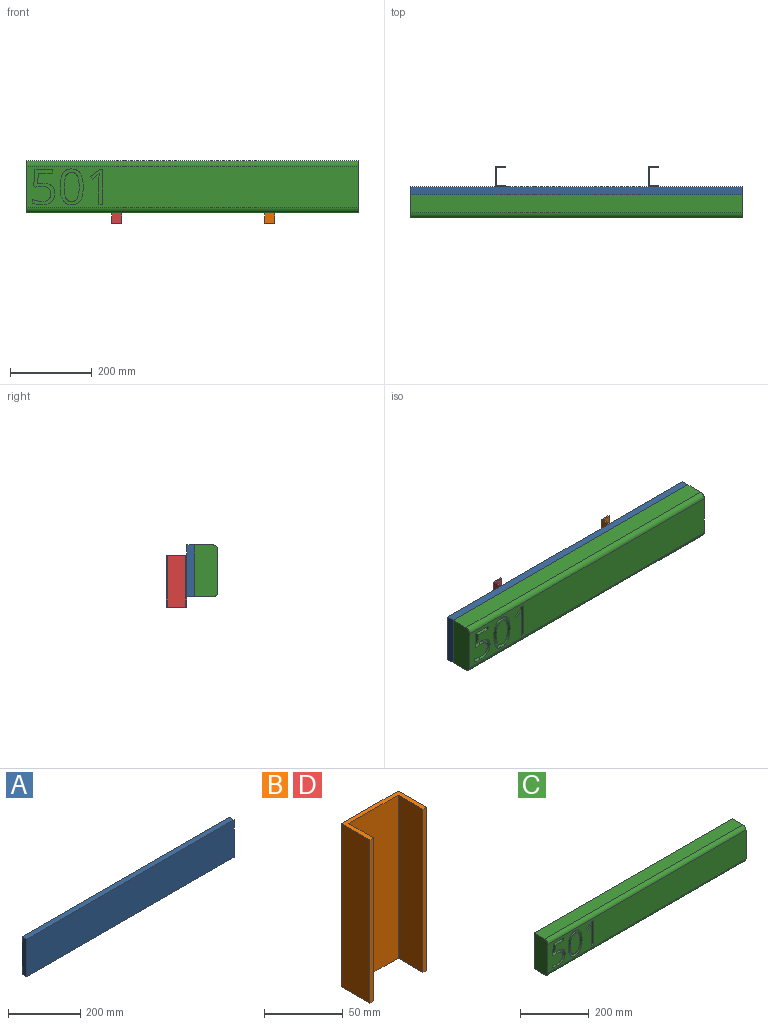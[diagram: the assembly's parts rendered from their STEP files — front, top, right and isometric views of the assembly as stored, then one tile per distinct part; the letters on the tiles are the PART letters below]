
ASSEMBLY  parts=4 mates=3
PART A: 6 faces, bbox 812.8x19.1x127 mm
  f0: plane 127x19.05mm, normal (1,0,0), area 2419.3mm2, adj f1,f3,f4,f5
  f1: plane 812.8x19.05mm, normal (0,0,1), area 15483.8mm2, adj f0,f2,f4,f5
  f2: plane 127x19.05mm, normal (-1,0,0), area 2419.3mm2, adj f1,f3,f4,f5
  f3: plane 812.8x19.05mm, normal (0,0,-1), area 15483.8mm2, adj f0,f2,f4,f5
  f4: plane 812.8x127mm, normal (0,-1,0), area 103225.6mm2, adj f0,f1,f2,f3
  f5: plane 812.8x127mm, normal (0,1,0), area 103225.6mm2, adj f0,f1,f2,f3
PART B: 10 faces, bbox 50.8x25.4x127 mm
  f0: plane 127x3.18mm, normal (0,-1,0), area 403.2mm2, adj f1,f6,f8,f9
  f1: plane 127x22.23mm, normal (1,0,0), area 2822.6mm2, adj f0,f2,f8,f9
  f2: plane 127x44.45mm, normal (0,-1,0), area 5645.2mm2, adj f1,f3,f8,f9
  f3: plane 127x22.23mm, normal (-1,0,0), area 2822.6mm2, adj f2,f7,f8,f9
  f4: plane 127x25.4mm, normal (1,0,0), area 3225.8mm2, adj f5,f7,f8,f9
  f5: plane 127x50.8mm, normal (0,1,0), area 6451.6mm2, adj f4,f6,f8,f9
  f6: plane 127x25.4mm, normal (-1,0,0), area 3225.8mm2, adj f0,f5,f8,f9
  f7: plane 127x3.18mm, normal (0,-1,0), area 403.2mm2, adj f3,f4,f8,f9
  f8: plane 50.8x25.4mm, normal (0,0,1), area 302.4mm2, adj f0,f1,f2,f3,f4,f5,f6,f7
  f9: plane 50.8x25.4mm, normal (0,0,-1), area 302.4mm2, adj f0,f1,f2,f3,f4,f5,f6,f7
PART C: 56 faces, bbox 812.8x57.2x127 mm
  f0: plane 812.8x101.6mm, normal (0,-1,0), area 75725.7mm2, adj f1,f3,f6,f7,f15,f16,f17,f18
  f1: plane 127x57.15mm, normal (1,0,0), area 7188.8mm2, adj f0,f2,f4,f5,f6,f7
  f2: plane 812.8x44.45mm, normal (0,0,1), area 36129mm2, adj f1,f3,f5,f6
  f3: plane 127x57.15mm, normal (-1,0,0), area 7188.8mm2, adj f0,f2,f4,f5,f6,f7
  f4: plane 812.8x44.45mm, normal (0,0,-1), area 36129mm2, adj f1,f3,f5,f7
  f5: plane 812.8x127mm, normal (0,1,0), area 103225.6mm2, adj f1,f2,f3,f4
  f6: cylinder r=12.7mm len=812.8mm, axis (1,0,0), area 16214.6mm2, adj f0,f1,f2,f3
  f7: cylinder r=12.7mm len=812.8mm, axis (-1,0,0), area 16214.6mm2, adj f0,f1,f3,f4
  f8: extruded ~27.2x10.16mm, area 282.3mm2, adj f9,f23,f24,f55
  f9: extruded ~27.14x10.16mm, area 281.6mm2, adj f8,f10,f24,f55
  f10: extruded ~13.98x10.16mm, area 175.8mm2, adj f9,f11,f24,f55
  f11: extruded ~14.08x10.16mm, area 177.5mm2, adj f10,f12,f24,f55
  f12: extruded ~27.01x10.16mm, area 280.3mm2, adj f11,f13,f24,f55
  f13: extruded ~27.09x10.16mm, area 281mm2, adj f12,f14,f24,f55
  f14: extruded ~14.08x10.16mm, area 177.9mm2, adj f13,f23,f24,f55
  f15: extruded ~33.15x10.16mm, area 348.6mm2, adj f0,f16,f22,f24
  f16: extruded ~32.72x10.16mm, area 344.9mm2, adj f0,f15,f17,f24
  f17: extruded ~21.17x11.31mm, area 255.5mm2, adj f0,f16,f18,f24
  f18: extruded ~21.24x10.84mm, area 253.8mm2, adj f0,f17,f19,f24
  f19: extruded ~33.19x10.16mm, area 348.9mm2, adj f0,f18,f20,f24
  f20: extruded ~32.89x10.16mm, area 346.5mm2, adj f0,f19,f21,f24
  f21: extruded ~21.01x11.21mm, area 253.5mm2, adj f0,f20,f22,f24
  f22: extruded ~21.4x10.95mm, area 255.9mm2, adj f0,f15,f21,f24
  f23: extruded ~13.98x10.16mm, area 176.2mm2, adj f8,f14,f24,f55
  f24: plane 88.12x56.61mm, normal (0,-1,0), area 1934.7mm2, adj f8,f9,f10,f11,f12,f13,f14,f15
  f25: plane 10.16x9.48mm, normal (0,0,1), area 96.3mm2, adj f0,f26,f33,f34
  f26: plane 85.59x10.16mm, normal (-1,0,0), area 869.6mm2, adj f0,f25,f27,f34
  f27: plane 10.16x8.19mm, normal (0,0,-1), area 83.2mm2, adj f0,f26,f28,f34
  f28: plane 22.65x17.52mm, normal (0.61,0,-0.79), area 290.9mm2, adj f0,f27,f29,f34
  f29: plane 10.16x6.67mm, normal (0.79,0,0.61), area 85.6mm2, adj f0,f28,f30,f34
  f30: extruded ~13.93x11.42mm, area 183mm2, adj f0,f29,f31,f34
  f31: extruded ~10.16x2.74mm, area 38.2mm2, adj f0,f30,f32,f34
  f32: extruded ~14.41x10.16mm, area 146.5mm2, adj f0,f31,f33,f34
  f33: plane 61x10.16mm, normal (1,0,0), area 619.7mm2, adj f0,f25,f32,f34
  f34: plane 85.59x30.84mm, normal (0,-1,0), area 1002.8mm2, adj f25,f26,f27,f28,f29,f30,f31,f32
  f35: extruded ~21.28x10.16mm, area 231.7mm2, adj f0,f36,f53,f54
  f36: extruded ~13.41x10.16mm, area 137.2mm2, adj f0,f35,f37,f54
  f37: plane 25.7x10.16mm, normal (-1,0,0.08), area 262.1mm2, adj f0,f36,f38,f54
  f38: plane 34.24x10.16mm, normal (0,0,1), area 347.9mm2, adj f0,f37,f39,f54
  f39: plane 10.16x8.95mm, normal (-1,0,0), area 91mm2, adj f0,f38,f40,f54
  f40: plane 42.56x10.16mm, normal (0,0,-1), area 432.4mm2, adj f0,f39,f41,f54
  f41: plane 40.05x10.16mm, normal (1,0,-0.08), area 408.2mm2, adj f0,f40,f42,f54
  f42: plane 10.16x5.04mm, normal (0.54,0,0.84), area 60.8mm2, adj f0,f41,f43,f54
  f43: extruded ~14.87x10.16mm, area 152.3mm2, adj f0,f42,f44,f54
  f44: extruded ~21.94x17.91mm, area 329.2mm2, adj f0,f43,f45,f54
  f45: extruded ~14.06x10.16mm, area 159.4mm2, adj f0,f44,f46,f54
  f46: extruded ~16.01x10.16mm, area 173.6mm2, adj f0,f45,f47,f54
  f47: extruded ~12.01x10.16mm, area 123.2mm2, adj f0,f46,f48,f54
  f48: extruded ~10.17x10.16mm, area 112mm2, adj f0,f47,f49,f54
  f49: plane 10.16x9.37mm, normal (1,0,0), area 95.2mm2, adj f0,f48,f50,f54
  f50: extruded ~22.07x10.16mm, area 231.8mm2, adj f0,f49,f51,f54
  f51: extruded ~23.33x10.16mm, area 254.9mm2, adj f0,f50,f52,f54
  f52: extruded ~20.84x10.16mm, area 235.9mm2, adj f0,f51,f53,f54
  f53: extruded ~18.36x10.16mm, area 209.3mm2, adj f0,f35,f52,f54
  f54: plane 86.77x53.86mm, normal (0,-1,0), area 1700.3mm2, adj f35,f36,f37,f38,f39,f40,f41,f42
  f55: plane 71.32x36.81mm, normal (0,-1,0), area 2217mm2, adj f8,f9,f10,f11,f12,f13,f14,f23
PART D: same geometry as B
PLACE A t=(-25.35,-28.05,-44.37)mm
PLACE B rot(axis=(0,0,1),90deg) t=(165.15,-2.65,-133.27)mm
PLACE C t=(-25.35,-28.05,-44.37)mm
PLACE D rot(axis=(0,0,1),90deg) t=(-209.6,-2.65,-133.27)mm
MATE fastened B.f6 <-> A.f5  axis (0,-1,0) through (177.85,-28.05,-6.27)mm
MATE fastened C.f5 <-> A.f4  axis (0,1,0) through (-25.35,-47.1,-44.37)mm
MATE fastened D.f6 <-> A.f5  axis (0,-1,0) through (-222.3,-28.05,-6.27)mm
